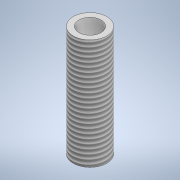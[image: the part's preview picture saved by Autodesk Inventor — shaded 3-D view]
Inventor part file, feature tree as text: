
AUTODESK INVENTOR PART (.ipt)
format: ipt  version: 2022 (Build 260153000, 153)  size: 114,688 bytes
history: native  units: mm
features: sketch x2, other x1, extrude x1, thread x1, hole x1
ambient origin geometry x8: Origin, YZ Plane, XZ Plane, XY Plane, X Axis, Y Axis, Z Axis, Center Point
bodies: Body1 (feature_tree)
feature tree (6):
  other  "Sólido1"
  extrude  "Extrusión1"  Depth=50.0mm TaperAngle=0.0deg
  thread  "Rosca1"  [1 undecoded]
  hole  "Agujero1"  [1 undecoded]
  sketch  "Boceto1"  dims[d0=15.164mm d1=50.0mm d2=0.0mm d3=45.0mm d4=0.0mm]
  sketch  "Boceto2"  dims[d5=10.0mm d6=10.0mm d7=4.0mm d8=2.0mm d9=90.0deg d10=8.0mm d11=20.594885mm]
note: 2 required parameter values undecoded (feature->parameter linkage not recoverable at this tier; creation-order binding heuristic only, values carry confidence <= 0.55)
